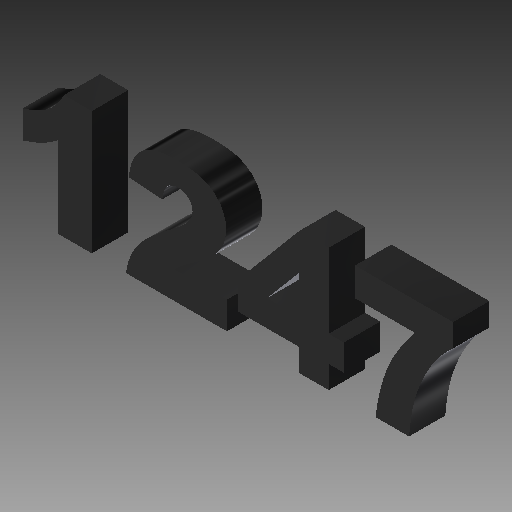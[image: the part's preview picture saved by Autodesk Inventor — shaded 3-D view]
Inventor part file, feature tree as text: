
AUTODESK INVENTOR PART (.ipt)
format: ipt  version: 2017.2 (Build 212233000, 233)  size: 807,936 bytes
history: native  units: in
note: dims shown in document units (in); Inventor stores cm internally (conversion verified against a paired STEP export)
features: sketch x24, extrude x18, projected_geometry x11, plane x9, loft x4, other x3, mirror x1, emboss x1, fillet x1
ambient origin geometry x8: Origin, YZ Plane, XZ Plane, XY Plane, X Axis, Y Axis, Z Axis, Center Point
bodies: Solid1 (feature_tree)
feature tree (72):
  sketch  "Sketch1"  dims[d0=0.7559in d1=0.7559in]
  plane  "Work Plane1"
  loft  "Loft1"
  extrude  "Extrusion1"  Depth=0.2in
  plane  "Work Plane4"
  loft  "Loft2"
  plane  "Work Plane5"
  loft  "Loft3"
  loft  "Loft4"
  extrude  "Extrusion2"  TaperAngle=0.0deg  [1 undecoded]
  plane  "Work Plane6"
  extrude  "Extrusion3"  Depth=1.0in
  extrude  "Extrusion4"  Depth=1.0651in
  extrude  "Extrusion5"  Depth=0.962in
  plane  "Work Plane7"
  extrude  "Extrusion6"  Depth=0.075in
  plane  "Work Plane8"
  other  "Work Axis1"
  plane  "Work Plane9"
  extrude  "Extrusion7"  Depth=0.06in
  mirror  "Mirror3"
  extrude  "Extrusion8"  Depth=0.05in
  plane  "Work Plane10"
  extrude  "Extrusion9"  Depth=0.0625in
  plane  "Work Plane11"
  extrude  "Extrusion10"  Depth=0.075in
  extrude  "Extrusion11"  TaperAngle=0.0deg  [1 undecoded]
  extrude  "Extrusion12"  Depth=0.2in
  extrude  "Extrusion13"  TaperAngle=0.0deg  [1 undecoded]
  emboss  "Emboss1"
  extrude  "Extrusion16"  Depth=0.01in
  extrude  "Extrusion17"  Depth=0.0344in
  extrude  "Extrusion18"  TaperAngle=60.0deg  [1 undecoded]
  fillet  "Fillet1"  [1 undecoded]
  extrude  "Extrusion19"  Depth=0.05in
  extrude  "Extrusion20"  Depth=0.05in
  sketch  "Sketch2"  dims[d2=0.9963in d3=0.2in]
  sketch  "Sketch3"  dims[d4=0.5in d6=0.08in]
  sketch  "Sketch4"  dims[d7=0.55in d8=150.0deg]
  other  "Edges1"
  sketch  "Sketch5"  dims[d9=150.0deg d14=0.33in]
  projected_geometry  "Projected Loop1"
  other  "Edges2"
  sketch  "Sketch6"  dims[d15=0.66in d18=0.0in d19=90.0deg]
  sketch  "Sketch7"  dims[d20=0.0in d21=90.0deg d22=1.0in]
  sketch  "Sketch8"  dims[d26=1.0651in d28=1.0651in]
  sketch  "Sketch9"  dims[d29=0.0in d30=0.962in]
  sketch  "Sketch10"  dims[d31=0.962in d32=0.075in]
  sketch  "Sketch11"  dims[d33=0.15in d34=0.06in]
  sketch  "Sketch12"  dims[d35=0.1in d36=0.05in]
  sketch  "Sketch13"  dims[d37=0.45in d38=0.0in d39=0.0625in]
  projected_geometry  "Projected Loop2"
  projected_geometry  "Projected Loop3"
  sketch  "Sketch14"  dims[d40=0.01in d41=0.075in]
  projected_geometry  "Projected Loop4"
  sketch  "Sketch15"  dims[d42=0.01in d43=0.0in d44=90.0deg]
  sketch  "Sketch16"  dims[d45=0.0in d46=90.0deg d47=0.2in]
  sketch  "Sketch17"  dims[d48=0.07in d49=0.0in d50=90.0deg]
  sketch  "Sketch18"  dims[d51=0.0in d52=90.0deg d53=0.01in]
  sketch  "Sketch19"  dims[d54=0.01in d55=0.0344in]
  sketch  "Sketch23"  dims[d56=150.0deg d57=60.0deg d58=150.0deg]
  projected_geometry  "Projected Loop6"
  sketch  "Sketch24"  dims[d59=0.7in d60=0.05in]
  sketch  "Sketch25"  dims[d61=0.05in d62=0.05in d63=0.05in]
  sketch  "Sketch26"  dims[d64=0.05in]
  projected_geometry  "Projected Loop7"
  projected_geometry  "Projected Loop8"
  sketch  "Sketch27"  dims[d65=0.01in d66=0.0in d67=90.0deg d68=0.0in d69=90.0deg d70=0.1in d71=0.4in d72=0.15in d73=0.05in d74=0.0in d75=0.02in d77=0.15in d78=0.02in d79=0.1in d80=0.1in d81=0.1in d82=0.02in d83=0.15in d84=0.05in d85=0.0in d86=0.045in d87=0.0in d88=0.025in d89=0.0in d90=0.02in d91=0.02in d92=0.005in d93=0.0in d94=90.0deg d95=0.4466in d96=1.0in d97=0.0in d98=1.0in d99=0.0in d100=0.6528in d101=0.0in d102=0.0in d103=1.0in d104=0.0in d106=90.0deg d107=1.0in d108=0.0in d109=1.65in d110=0.1in d111=0.1in d112=0.0in d113=0.1in d114=0.075in d115=0.0in d116=0.05in d117=0.0in d123=0.84in d124=0.8in d125=0.0in d126=0.0in d127=1.0in d128=0.0in d130=0.15in d131=-0.0206in d135=0.2in d136=0.05in d137=0.1in d138=0.05in d139=0.0in d140=0.025in d141=0.0in]
  projected_geometry  "Projected Loop9"
  projected_geometry  "Projected Loop10"
  projected_geometry  "Projected Loop11"
  projected_geometry  "Projected Loop12"
note: 5 required parameter values undecoded (feature->parameter linkage not recoverable at this tier; creation-order binding heuristic only, values carry confidence <= 0.55)
